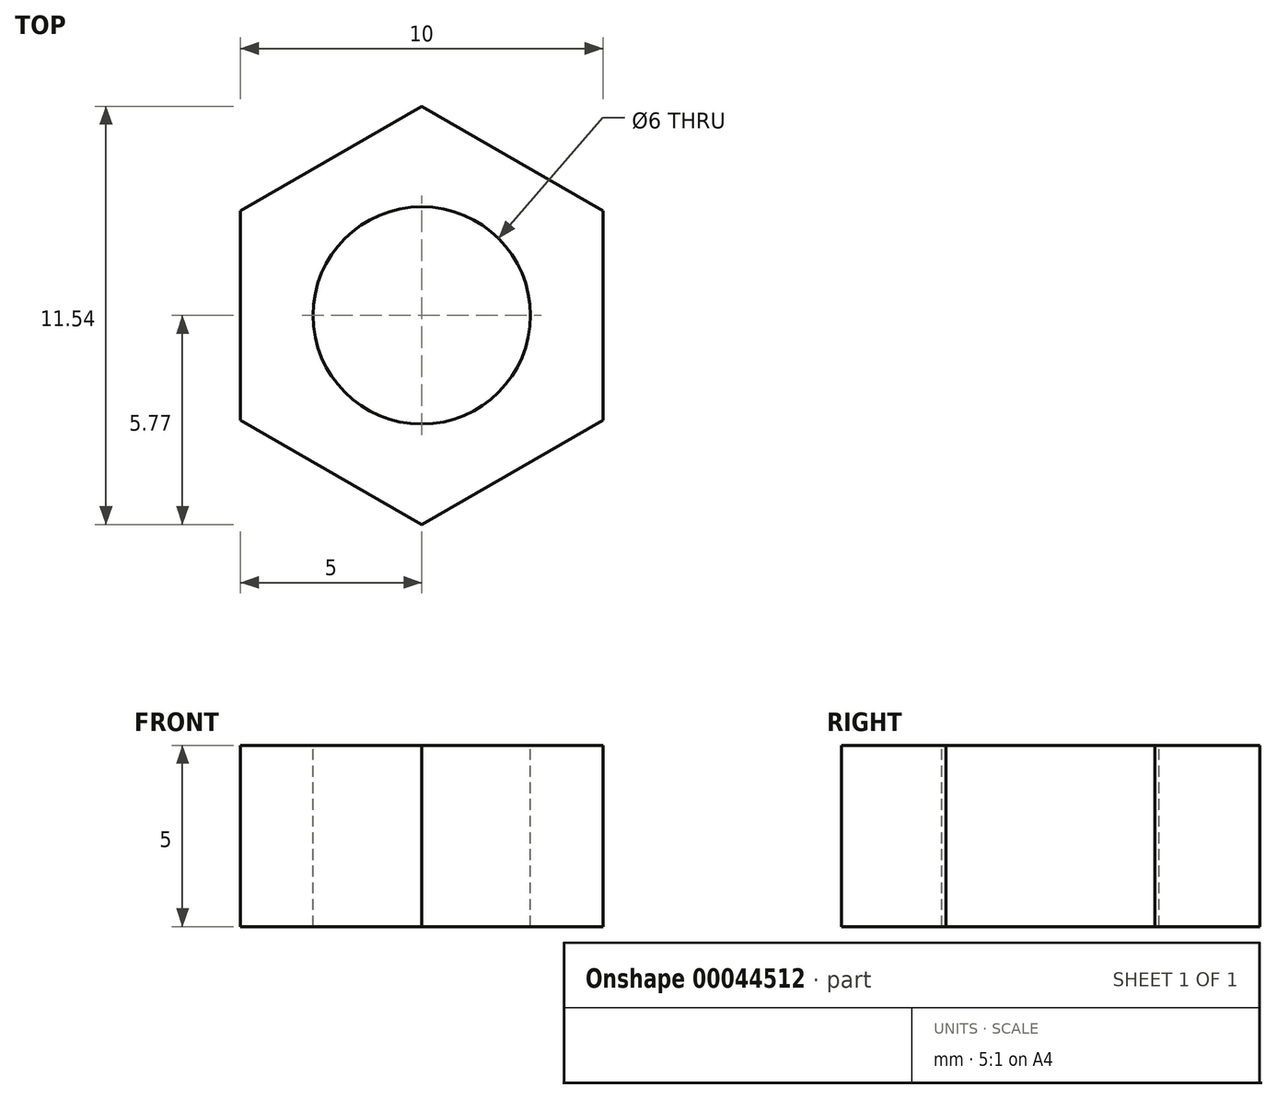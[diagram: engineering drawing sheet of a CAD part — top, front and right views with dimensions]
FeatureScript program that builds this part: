
annotation { "Feature Type Name" : "Feature", "Feature Type Description" : "" }
export const myFeature = defineFeature(function(context is Context, id is Id, definition is map)
    precondition{}
    {
        {
            var Q0;
            Q0=qCreatedBy(makeId("Top.planeOp"),FACE);
            var sketch = newSketch(context, id + "F0", { "sketchPlane" : qUnion([Q0])});
            skCircle(sketch, "E0.cCircle", {"center": v(0, 0) * mm, "radius": 5 * mm, "construction": true});
            skLineSegment(sketch, "E0.0", {"start": v(-5, 2.89) * mm, "end": v(0, 5.77) * mm});
            skLineSegment(sketch, "E0.1", {"start": v(0, 5.77) * mm, "end": v(5, 2.89) * mm});
            skLineSegment(sketch, "E0.2", {"start": v(5, 2.89) * mm, "end": v(5, -2.89) * mm});
            skLineSegment(sketch, "E0.3", {"start": v(5, -2.89) * mm, "end": v(0, -5.77) * mm});
            skLineSegment(sketch, "E0.4", {"start": v(0, -5.77) * mm, "end": v(-5, -2.89) * mm});
            skLineSegment(sketch, "E0.5", {"start": v(-5, -2.89) * mm, "end": v(-5, 2.89) * mm});
            skPoint(sketch, "E0.0.midPoint", {"position": v(-2.5, 4.33) * mm});
            skSolve(sketch);
        }
        {
            var Q0;
            Q0=makeQuery(id+"F0.imprint","IMPRINT",FACE,{"disambiguationData":[TD([[makeQuery(id+"F0.imprint","IMPRINT",EDGE,{"derivedFrom":sQuery(id+"F0.wireOp",EDGE,"E0.0")}),-1.0]])]});
            extrude(context, id + "F1", {"entities" : qUnion([Q0]), "depth" : 5 * mm});
        }
        {
            var Q0;
            Q0=makeQuery(id+"F1.opExtrude","CAP_FACE",FACE,{"disambiguationData":[OSD([sQuery(id+"F0.wireOp",EDGE,"E0.0"),sQuery(id+"F0.wireOp",EDGE,"E0.1"),sQuery(id+"F0.wireOp",EDGE,"E0.2"),sQuery(id+"F0.wireOp",EDGE,"E0.3"),sQuery(id+"F0.wireOp",EDGE,"E0.4"),sQuery(id+"F0.wireOp",EDGE,"E0.5")])],"isStart":false});
            var sketch = newSketch(context, id + "F2", { "sketchPlane" : qUnion([Q0])});
            skPoint(sketch, "E1", {"position": v(0, 0) * mm});
            skSolve(sketch);
        }
        {
            var Q0;
            Q0=sQuery(id+"F2.wireOp",VERTEX,"E1");
            var Q1;
            Q1=makeQuery(id+"F1.opExtrude","SWEPT_BODY",BODY,{"disambiguationData":[OSD([sQuery(id+"F0.wireOp",EDGE,"E0.0"),sQuery(id+"F0.wireOp",EDGE,"E0.1"),sQuery(id+"F0.wireOp",EDGE,"E0.2"),sQuery(id+"F0.wireOp",EDGE,"E0.3"),sQuery(id+"F0.wireOp",EDGE,"E0.4"),sQuery(id+"F0.wireOp",EDGE,"E0.5")])]});
            hole(context, id + "F3", {"style" : HoleStyle.SIMPLE, "holeDiameter" : 6 * mm, "endStyle" : HoleEndStyle.THROUGH, "locations" : qUnion([Q0]), "scope" : qUnion([Q1])});
        }
    });
